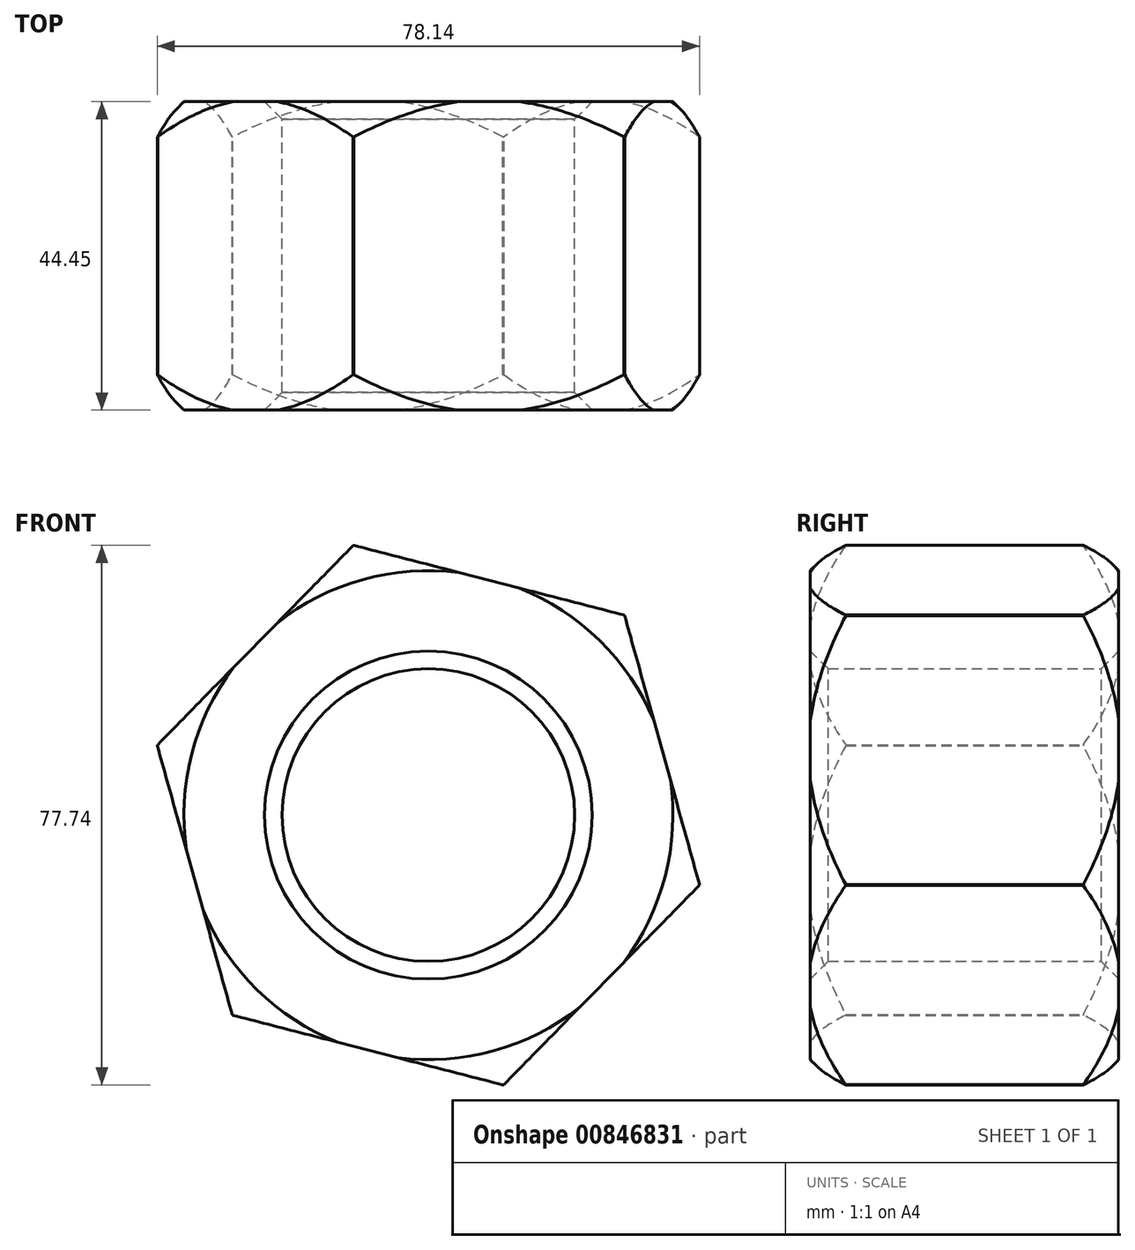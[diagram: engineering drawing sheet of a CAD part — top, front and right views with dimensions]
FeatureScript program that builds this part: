
annotation { "Feature Type Name" : "Feature", "Feature Type Description" : "" }
export const myFeature = defineFeature(function(context is Context, id is Id, definition is map)
    precondition{}
    {
        {
            var Q0;
            Q0=qCreatedBy(makeId("Front.planeOp"),FACE);
            var sketch = newSketch(context, id + "F0", { "sketchPlane" : qUnion([Q0])});
            skCircle(sketch, "E0.cCircle", {"center": v(0, 0) * mm, "radius": 34.92 * mm, "construction": true});
            skLineSegment(sketch, "E0.0", {"start": v(40.32, -0.87) * mm, "end": v(19.4, -35.35) * mm, "construction": true});
            skLineSegment(sketch, "E0.1", {"start": v(19.4, -35.35) * mm, "end": v(-20.92, -34.48) * mm, "construction": true});
            skLineSegment(sketch, "E0.2", {"start": v(-20.92, -34.48) * mm, "end": v(-40.32, 0.87) * mm, "construction": true});
            skLineSegment(sketch, "E0.3", {"start": v(-40.32, 0.87) * mm, "end": v(-19.4, 35.35) * mm, "construction": true});
            skLineSegment(sketch, "E0.4", {"start": v(-19.4, 35.35) * mm, "end": v(20.92, 34.48) * mm, "construction": true});
            skLineSegment(sketch, "E0.5", {"start": v(20.92, 34.48) * mm, "end": v(40.32, -0.87) * mm, "construction": true});
            skPoint(sketch, "E0.0.midPoint", {"position": v(29.86, -18.11) * mm});
            skCircle(sketch, "E1", {"center": v(0, 0) * mm, "radius": 21.08 * mm});
            skCircle(sketch, "E2", {"center": v(0, 0) * mm, "radius": 40.33 * mm});
            skSolve(sketch);
        }
        {
            var Q0;
            Q0 = qSketchRegion(id + "F0", true);
            extrude(context, id + "F1", {"entities" : qUnion([Q0]), "depth" : 44.45 * mm, "offsetDistance" : 25.4 * mm});
        }
        {
            var Q0;
            Q0=makeQuery(id+"F1.opExtrude","SWEPT_FACE",FACE,{"disambiguationData":[OSD([sQuery(id+"F0.wireOp",EDGE,"E1")])]});
            chamfer(context, id + "F2", {"entities" : qUnion([Q0]), "width" : 2.54 * mm, "tangentPropagation" : true});
        }
        {
            var Q0;
            Q0=makeQuery(id+"F1.opExtrude","SWEPT_FACE",FACE,{"disambiguationData":[OSD([sQuery(id+"F0.wireOp",EDGE,"E2")])]});
            chamfer(context, id + "F3", {"entities" : qUnion([Q0]), "width" : 5.08 * mm, "tangentPropagation" : true});
        }
        {
            var Q0;
            Q0=qCreatedBy(makeId("Front.planeOp"),FACE);
            var sketch = newSketch(context, id + "F4", { "sketchPlane" : qUnion([Q0])});
            skCircle(sketch, "E3.cCircle", {"center": v(0, 0) * mm, "radius": 34.96 * mm, "construction": true});
            skLineSegment(sketch, "E3.0", {"start": v(39.1, -10.08) * mm, "end": v(10.82, -38.9) * mm});
            skLineSegment(sketch, "E3.1", {"start": v(10.82, -38.9) * mm, "end": v(-28.28, -28.82) * mm});
            skLineSegment(sketch, "E3.2", {"start": v(-28.28, -28.82) * mm, "end": v(-39.1, 10.08) * mm});
            skLineSegment(sketch, "E3.3", {"start": v(-39.1, 10.08) * mm, "end": v(-10.82, 38.9) * mm});
            skLineSegment(sketch, "E3.4", {"start": v(-10.82, 38.9) * mm, "end": v(28.28, 28.82) * mm});
            skLineSegment(sketch, "E3.5", {"start": v(28.28, 28.82) * mm, "end": v(39.1, -10.08) * mm});
            skPoint(sketch, "E3.0.midPoint", {"position": v(24.96, -24.49) * mm});
            skCircle(sketch, "E4", {"center": v(0, 0) * mm, "radius": 70 * mm});
            skSolve(sketch);
        }
        {
            var Q0;
            Q0 = qSketchRegion(id + "F4", true);
            extrude(context, id + "F5", {"entities" : qUnion([Q0]), "operationType" : NewBodyOperationType.REMOVE, "endBound" : BoundingType.THROUGH_ALL, "depth" : 25.4 * mm, "offsetDistance" : 25.4 * mm});
        }
    });
